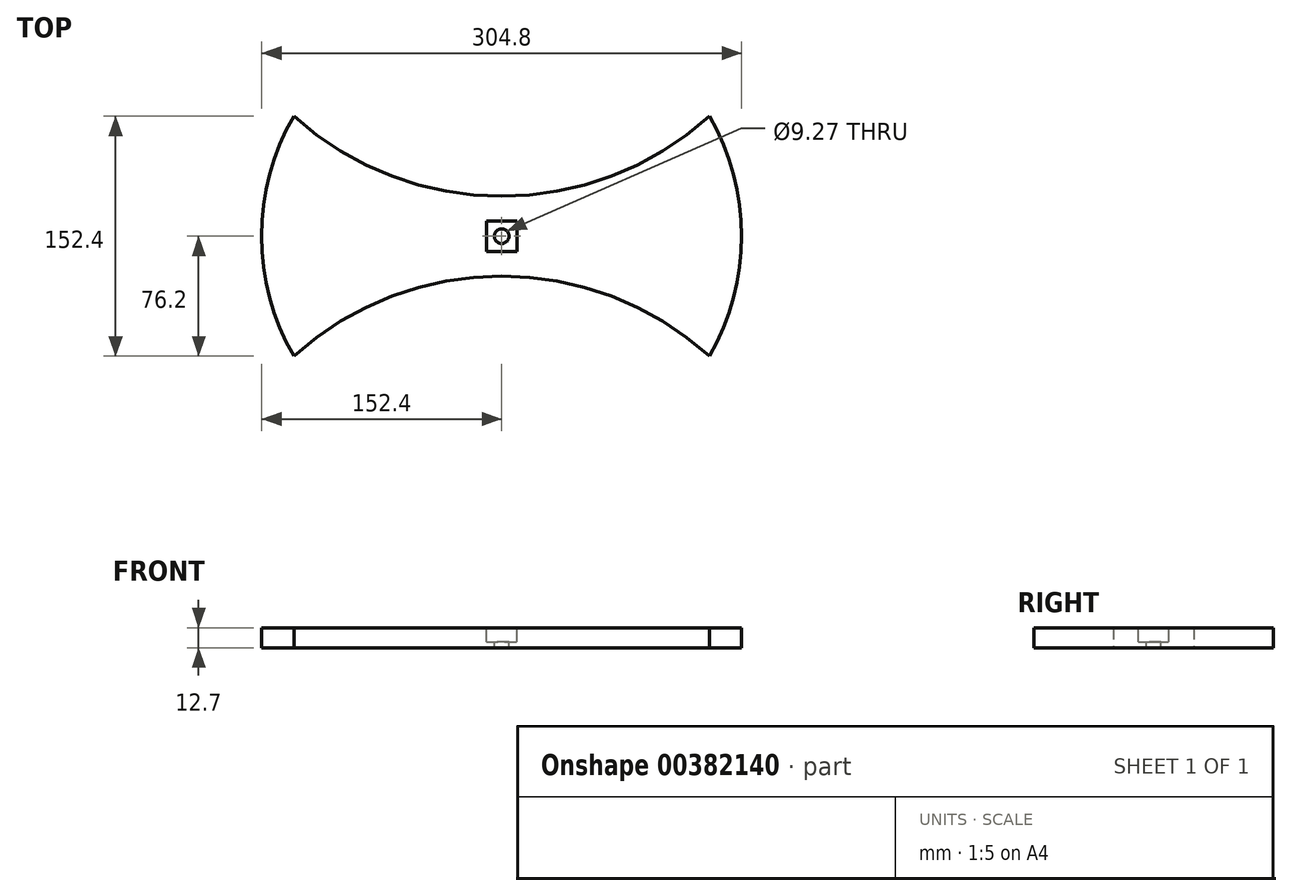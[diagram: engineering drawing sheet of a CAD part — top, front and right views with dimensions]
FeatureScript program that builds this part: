
annotation { "Feature Type Name" : "Feature", "Feature Type Description" : "" }
export const myFeature = defineFeature(function(context is Context, id is Id, definition is map)
    precondition{}
    {
        {
            var Q0;
            Q0=qCreatedBy(makeId("Top.planeOp"),FACE);
            var sketch = newSketch(context, id + "F0", { "sketchPlane" : qUnion([Q0])});
            skCircle(sketch, "E0", {"center": v(0, 0) * mm, "radius": 152.4 * mm});
            skLineSegment(sketch, "E1", {"start": v(0, 0) * mm, "end": v(0, 25.4) * mm});
            skLineSegment(sketch, "E2", {"start": v(0, 25.4) * mm, "end": v(0, 222.25) * mm});
            skCircle(sketch, "E3", {"center": v(0, 222.25) * mm, "radius": 196.85 * mm});
            skCircle(sketch, "E4.MirrorC", {"center": v(0, -222.25) * mm, "radius": 196.85 * mm});
            skSolve(sketch);
        }
        {
            var Q0;
            {var subQ0=sQuery(id+"F0.wireOp",EDGE,"E3");var subQ1=sQuery(id+"F0.wireOp",EDGE,"E0");var subQ2=makeQuery(id+"F0.imprint","INTERSECT",VERTEX,{"disambiguationData":[OD(0.0)],"derivedFrom":[subQ1,subQ0]});Q0=makeQuery(id+"F0.imprint","IMPRINT",FACE,{"disambiguationData":[TD([[makeQuery(id+"F0.imprint","IMPRINT",EDGE,{"disambiguationData":[TD([[subQ2,1.0]])],"derivedFrom":subQ1}),1.0]])]});}
            extrude(context, id + "F1", {"entities" : qUnion([Q0]), "depth" : 12.7 * mm});
        }
        {
            var Q0;
            Q0=makeQuery(id+"F1.opExtrude","CAP_FACE",FACE,{"disambiguationData":[OSD([sQuery(id+"F0.wireOp",EDGE,"E0"),sQuery(id+"F0.wireOp",EDGE,"E3"),sQuery(id+"F0.wireOp",EDGE,"E4.MirrorC")])],"isStart":false});
            var sketch = newSketch(context, id + "F2", { "sketchPlane" : qUnion([Q0])});
            skCircle(sketch, "E5", {"center": v(0, 0) * mm, "radius": 4.64 * mm});
            skSolve(sketch);
        }
        {
            var Q0;
            Q0=qSketchRegion(id+"F2",true);
            extrude(context, id + "F3", {"entities" : qUnion([Q0]), "operationType" : NewBodyOperationType.REMOVE, "endBound" : BoundingType.UP_TO_NEXT, "oppositeDirection" : true, "depth" : 25.4 * mm});
        }
        {
            var Q0;
            Q0=makeQuery(id+"F1.opExtrude","CAP_FACE",FACE,{"disambiguationData":[OSD([sQuery(id+"F0.wireOp",EDGE,"E0"),sQuery(id+"F0.wireOp",EDGE,"E3"),sQuery(id+"F0.wireOp",EDGE,"E4.MirrorC")])],"isStart":false});
            var sketch = newSketch(context, id + "F4", { "sketchPlane" : qUnion([Q0])});
            skLineSegment(sketch, "E6.bottom", {"start": v(-9.65, -9.65) * mm, "end": v(9.65, -9.65) * mm});
            skLineSegment(sketch, "E6.top", {"start": v(-9.65, 9.65) * mm, "end": v(9.65, 9.65) * mm});
            skLineSegment(sketch, "E6.left", {"start": v(-9.65, -9.65) * mm, "end": v(-9.65, 9.65) * mm});
            skLineSegment(sketch, "E6.right", {"start": v(9.65, -9.65) * mm, "end": v(9.65, 9.65) * mm});
            skPoint(sketch, "E6.middle", {"position": v(0, 0) * mm});
            skSolve(sketch);
        }
        {
            var Q0;
            Q0=makeQuery(id+"F4.imprint","IMPRINT",FACE,{"disambiguationData":[TD([[makeQuery(id+"F4.imprint","IMPRINT",EDGE,{"derivedFrom":sQuery(id+"F4.wireOp",EDGE,"E6.bottom")}),1.0]])]});
            extrude(context, id + "F5", {"entities" : qUnion([Q0]), "operationType" : NewBodyOperationType.REMOVE, "oppositeDirection" : true, "depth" : 8.9 * mm});
        }
    });
